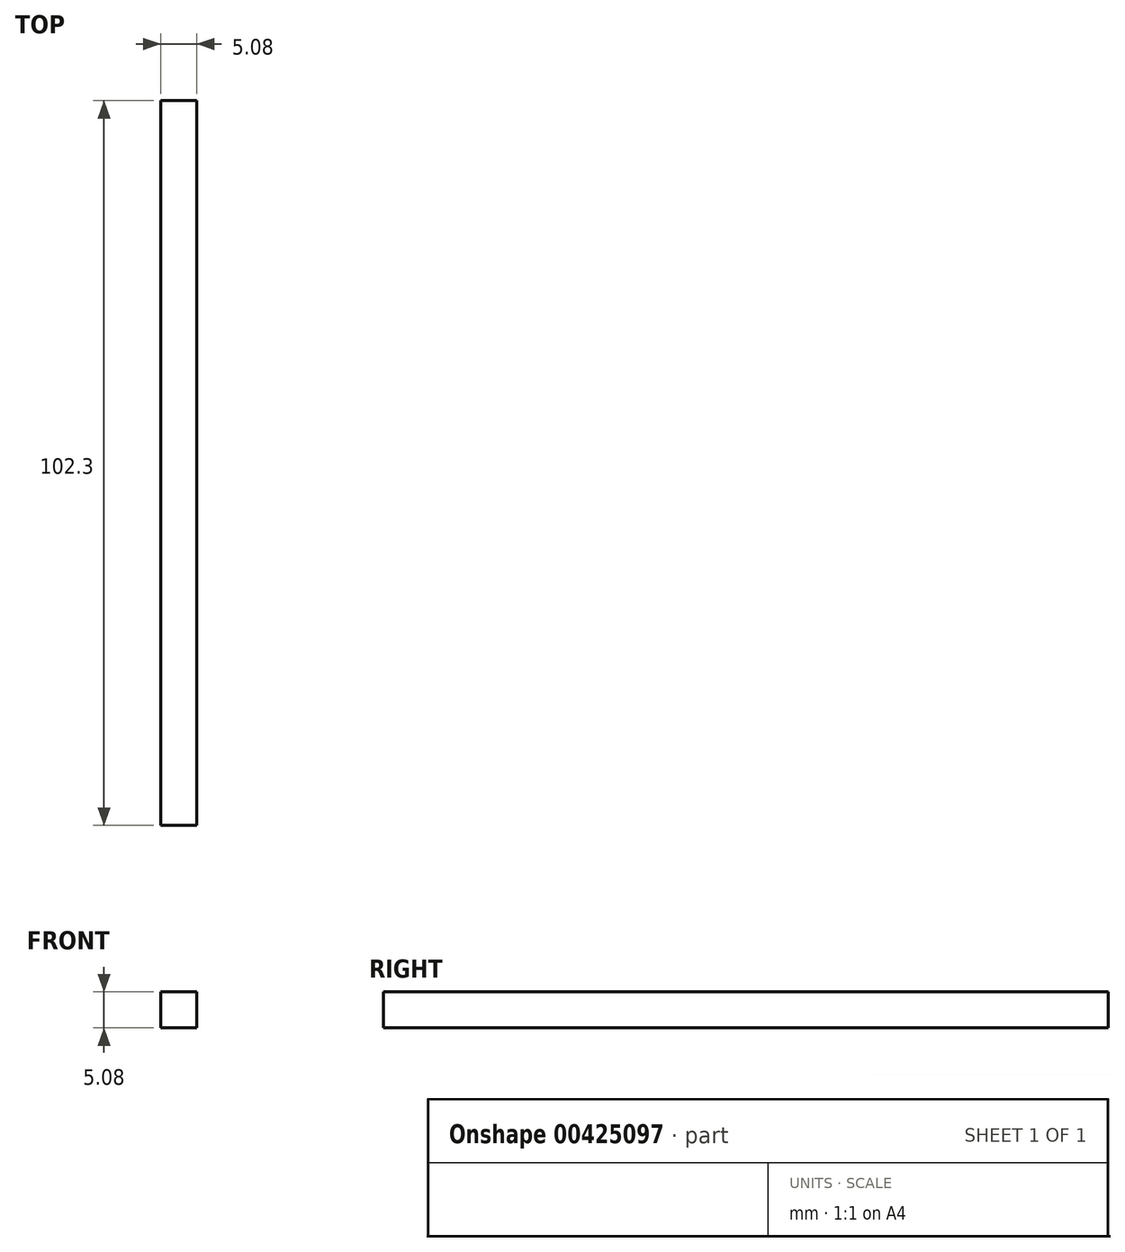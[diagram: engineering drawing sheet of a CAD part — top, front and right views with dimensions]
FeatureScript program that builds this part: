
annotation { "Feature Type Name" : "Feature", "Feature Type Description" : "" }
export const myFeature = defineFeature(function(context is Context, id is Id, definition is map)
    precondition{}
    {
        {
            var Q0;
            Q0=qCreatedBy(makeId("Front.planeOp"),FACE);
            var sketch = newSketch(context, id + "F0", { "sketchPlane" : qUnion([Q0])});
            skLineSegment(sketch, "E0.bottom", {"start": v(-30.3, 28.27) * mm, "end": v(-25.22, 28.27) * mm});
            skLineSegment(sketch, "E0.top", {"start": v(-30.3, 23.2) * mm, "end": v(-25.22, 23.2) * mm});
            skLineSegment(sketch, "E0.left", {"start": v(-30.3, 28.27) * mm, "end": v(-30.3, 23.2) * mm});
            skLineSegment(sketch, "E0.right", {"start": v(-25.22, 28.27) * mm, "end": v(-25.22, 23.2) * mm});
            skSolve(sketch);
        }
        {
            var Q0;
            Q0 = qSketchRegion(id + "F0", true);
            extrude(context, id + "F1", {"entities" : qUnion([Q0]), "depth" : 102.3 * mm, "offsetDistance" : 25.4 * mm});
        }
    });
